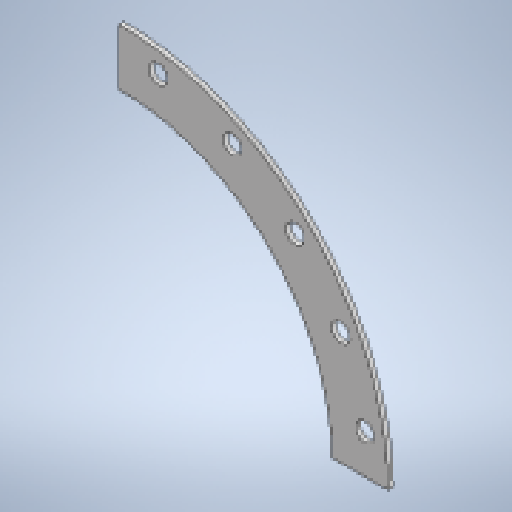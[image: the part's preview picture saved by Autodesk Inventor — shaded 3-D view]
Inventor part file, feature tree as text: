
AUTODESK INVENTOR PART (.ipt)
format: ipt  version: 2025.1 (Build 291241020, 241B)  size: 204,288 bytes
history: native  units: mm
features: sketch x2, other x2, extrude x1, pattern_circular x1, projected_geometry x1
ambient origin geometry x8: Origin, YZ Plane, XZ Plane, XY Plane, X Axis, Y Axis, Z Axis, Center Point
bodies: Solid1 (feature_tree)
feature tree (7):
  extrude  "Extrusion1"  Depth=6.0mm TaperAngle=0.0deg
  pattern_circular  "Circular Pattern1"  Count=53  [1 undecoded]
  sketch  "Sketch1"  dims[d0=512.0mm d1=670.0mm d2=6.0mm d3=0.0mm d4=530.0mm]
  sketch  "Sketch2"  dims[d5=310.0mm d6=1.570796mm d7=23.0mm d8=8.0mm d9=8.0mm d10=0.0mm d11=200.0mm d12=360.0deg]
  projected_geometry  "Projected Loop1"
  other  "Cut1"
  other  "Definition1"
note: 1 required parameter value undecoded (feature->parameter linkage not recoverable at this tier; creation-order binding heuristic only, values carry confidence <= 0.55)
